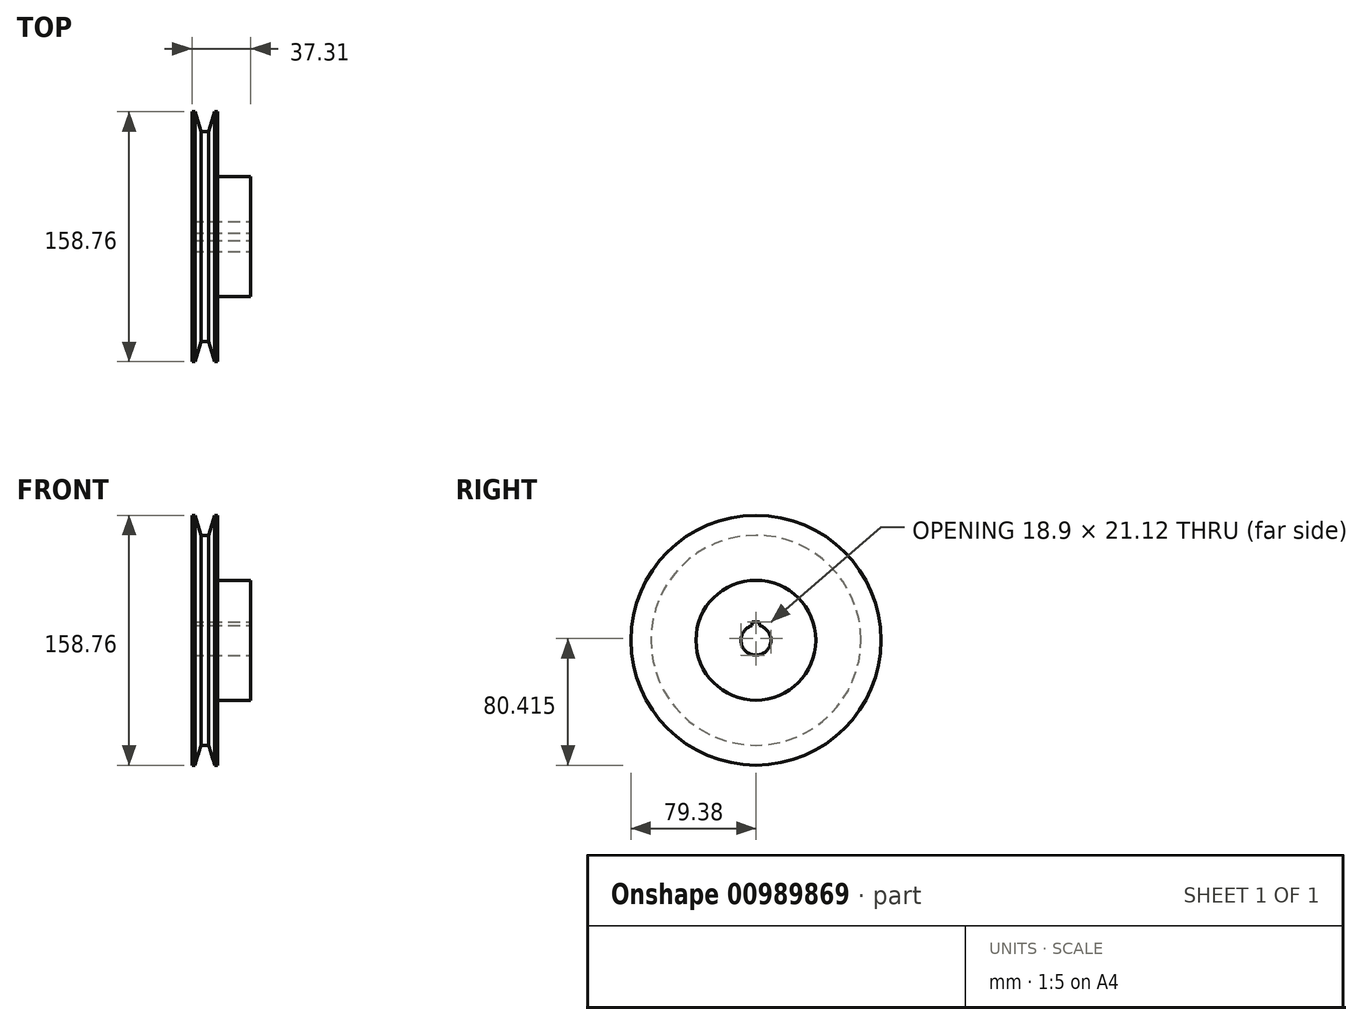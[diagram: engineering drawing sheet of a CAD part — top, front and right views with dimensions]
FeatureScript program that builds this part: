
annotation { "Feature Type Name" : "Feature", "Feature Type Description" : "" }
export const myFeature = defineFeature(function(context is Context, id is Id, definition is map)
    precondition{}
    {
        {
            var Q0;
            Q0=qCreatedBy(makeId("Front.planeOp"),FACE);
            var sketch = newSketch(context, id + "F0", { "sketchPlane" : qUnion([Q0])});
            skLineSegment(sketch, "E0", {"start": v(8.14, 9.53) * mm, "end": v(-8.14, 9.53) * mm});
            skLineSegment(sketch, "E1", {"start": v(-8.14, 9.52) * mm, "end": v(-8.14, 79.38) * mm});
            skLineSegment(sketch, "E2", {"start": v(-6.27, 79.38) * mm, "end": v(-8.14, 79.38) * mm});
            skLineSegment(sketch, "E3", {"start": v(-6.27, 79.38) * mm, "end": v(-2.4, 66.68) * mm});
            skLineSegment(sketch, "E4", {"start": v(-2.4, 66.68) * mm, "end": v(2.4, 66.68) * mm});
            skLineSegment(sketch, "E5", {"start": v(2.4, 66.68) * mm, "end": v(6.27, 79.38) * mm});
            skLineSegment(sketch, "E6", {"start": v(6.27, 79.38) * mm, "end": v(8.14, 79.38) * mm});
            skLineSegment(sketch, "E7", {"start": v(8.14, 79.38) * mm, "end": v(8.14, 38.1) * mm});
            skLineSegment(sketch, "E8", {"start": v(0, 66.68) * mm, "end": v(0, 0) * mm, "construction": true});
            skPoint(sketch, "E9", {"position": v(0, 9.53) * mm});
            skLineSegment(sketch, "E10", {"start": v(0, 0) * mm, "end": v(-51.93, 0) * mm, "construction": true});
            skLineSegment(sketch, "E11.bottom", {"start": v(8.14, 9.53) * mm, "end": v(29.17, 9.53) * mm});
            skLineSegment(sketch, "E11.top", {"start": v(8.14, 38.1) * mm, "end": v(29.17, 38.1) * mm});
            skLineSegment(sketch, "E11.right", {"start": v(29.17, 9.53) * mm, "end": v(29.17, 38.1) * mm});
            skSolve(sketch);
        }
        {
            var Q0;
            Q0 = qSketchRegion(id + "F0", true);
            var Q1;
            Q1=sQuery(id+"F0.wireOp",EDGE,"E10");
            revolve(context, id + "F1", {"surfaceOperationType" : NewSurfaceOperationType.NEW, "entities" : qUnion([Q0]), "axis" : qUnion([Q1]), "revolveType" : RevolveType.FULL});
        }
        {
            var Q0;
            Q0=qCreatedBy(makeId("Right.planeOp"),FACE);
            var sketch = newSketch(context, id + "F2", { "sketchPlane" : qUnion([Q0])});
            skLineSegment(sketch, "E12.bottom", {"start": v(-2.38, 11.6) * mm, "end": v(2.38, 11.6) * mm});
            skLineSegment(sketch, "E12.left", {"start": v(-2.38, 11.6) * mm, "end": v(-2.38, 9.22) * mm});
            skLineSegment(sketch, "E12.right", {"start": v(2.38, 11.6) * mm, "end": v(2.38, 9.22) * mm});
            skArc(sketch, "E13.0", {"start": v(-2.38, 9.22) * mm, "mid": v(0, -9.53) * mm, "end": v(2.38, 9.22) * mm});
            skLineSegment(sketch, "E14", {"start": v(0, 0) * mm, "end": v(0, 11.6) * mm, "construction": true});
            skCircle(sketch, "E15", {"center": v(0, 0) * mm, "radius": 9.53 * mm, "construction": true});
            skPoint(sketch, "E16", {"position": v(0, 9.53) * mm});
            skLineSegment(sketch, "E17", {"start": v(-2.38, 6.83) * mm, "end": v(2.38, 6.83) * mm, "construction": true});
            skSolve(sketch);
        }
        {
            var Q0;
            Q0 = qSketchRegion(id + "F2", true);
            extrude(context, id + "F3", {"entities" : qUnion([Q0]), "operationType" : NewBodyOperationType.REMOVE, "endBound" : BoundingType.THROUGH_ALL, "oppositeDirection" : true, "depth" : 25.4 * mm, "offsetDistance" : 25.4 * mm, "hasSecondDirection" : true, "secondDirectionBound" : SecondDirectionBoundingType.THROUGH_ALL, "secondDirectionOppositeDirection" : false, "secondDirectionDepth" : 25.4 * mm});
        }
    });
